# Revit family: VL2S-GFS150xSIxMPx
name_source: partatom
category: Leuchten
units: mm (PartAtom-declared; Revit-internal decimal feet)

## family parameters
Basisbauteil = Fläche
Beim Laden mit Abzugskörper schneiden = Nein
Bemaßung runder Anschluss = Durchmesser verwenden
Gemeinsam genutzt = Nein
Lichtquelle = Ja
OmniClass-Nummer = 23.80.70.11
OmniClass-Titel = Luminaries for Internal Lighting
Raumberechnungspunkt = Nein
Teiletyp = Normal

## types (16) — shared parameters
Baugruppenkennzeichen = D5020200
Datei für fotometrisches Netz = VL2S-GFS_MP.IES
Emissionsform beim Rendern sichtbar = Nein
Farbfilter = 16777215
Farbtemperaturverschiebung bei Dämpfen der Lampe = <Keine Auswahl>
Hersteller = RIDI Leuchten GmbH
Lampe = LED
Neigungswinkel = 90.00°
URL = www.ridi.de
Von Breite des Rechtecks ausssenden = 1477 mm  [stored 4.8458 ft]
Von Länge des Rechtecks aussenden = 85 mm  [stored 0.278871 ft]
brand = RIDI
conformity mark = CE
electrical safety class = 1
height = 77 mm  [stored 0.252625 ft]
ingress protection (IP) code = IP54
length = 1500 mm  [stored 4.92126 ft]
nominal frequency = 50-60Hz
nominal voltage = 230
voltage type (AC, DC, UC) = AC
width = 97 mm  [stored 0.318241 ft]
zero-valued in all types: Vorgabe-Ansicht

## per-type parameters (varying)
| type | Modell | Scheinlast | rated input power | weight |
| VL2S-GFS150-5FLSI840MP0750 | 2550139SI | 53 VA | 53 | 2,9 kg |
| VL2S-GFS150-5FLSI840MP1600 | 2550142SI | 103 VA | 103 | 3,3 kg |
| VL2S-GFS150-5FLSI830MP0750 | 2550148SI | 53 VA | 53 | 2,9 kg |
| VL2S-GFS150-5FLSI830MP1500 | 2550151SI | 103 VA | 103 | 3,3 kg |
| VL2S-GFS150-5FLSI850MP0750 | 2550154SI | 53 VA | 53 | 2,9 kg |
| VL2S-GFS150-5FLSI850MP1600 | 2550157SI | 103 VA | 103 | 3,3 kg |
| VL2S-GFS150-5FLSI865MP0750 | 2550160SI | 53 VA | 53 | 2,9 kg |
| VL2S-GFS150-5FLSI865MP1500 | 2550163SI | 103 VA | 103 | 3,3 kg |
| VL2S-GFS150-7DASI840MP0750 | 2560139SI | 52 VA | 52 | 2,9 kg |
| VL2S-GFS150-7DASI840MP1600 | 2560142SI | 102 VA | 102 | 3,3 kg |
| VL2S-GFS150-7DASI830MP0750 | 2560148SI | 52 VA | 52 | 2,9 kg |
| VL2S-GFS150-7DASI830MP1500 | 2560151SI | 102 VA | 102 | 3,3 kg |
| VL2S-GFS150-7DASI850MP0750 | 2560154SI | 52 VA | 52 | 2,9 kg |
| VL2S-GFS150-7DASI850MP1600 | 2560157SI | 102 VA | 102 | 3,3 kg |
| VL2S-GFS150-7DASI865MP0750 | 2560160SI | 52 VA | 52 | 2,9 kg |
| VL2S-GFS150-7DASI865MP1500 | 2560163SI | 102 VA | 102 | 3,3 kg |

note: column(s) folded — value = type name in every type: product name

note: [stored X ft] marks values corroborated as IEEE doubles in the binary element streams (Revit-internal decimal feet)
